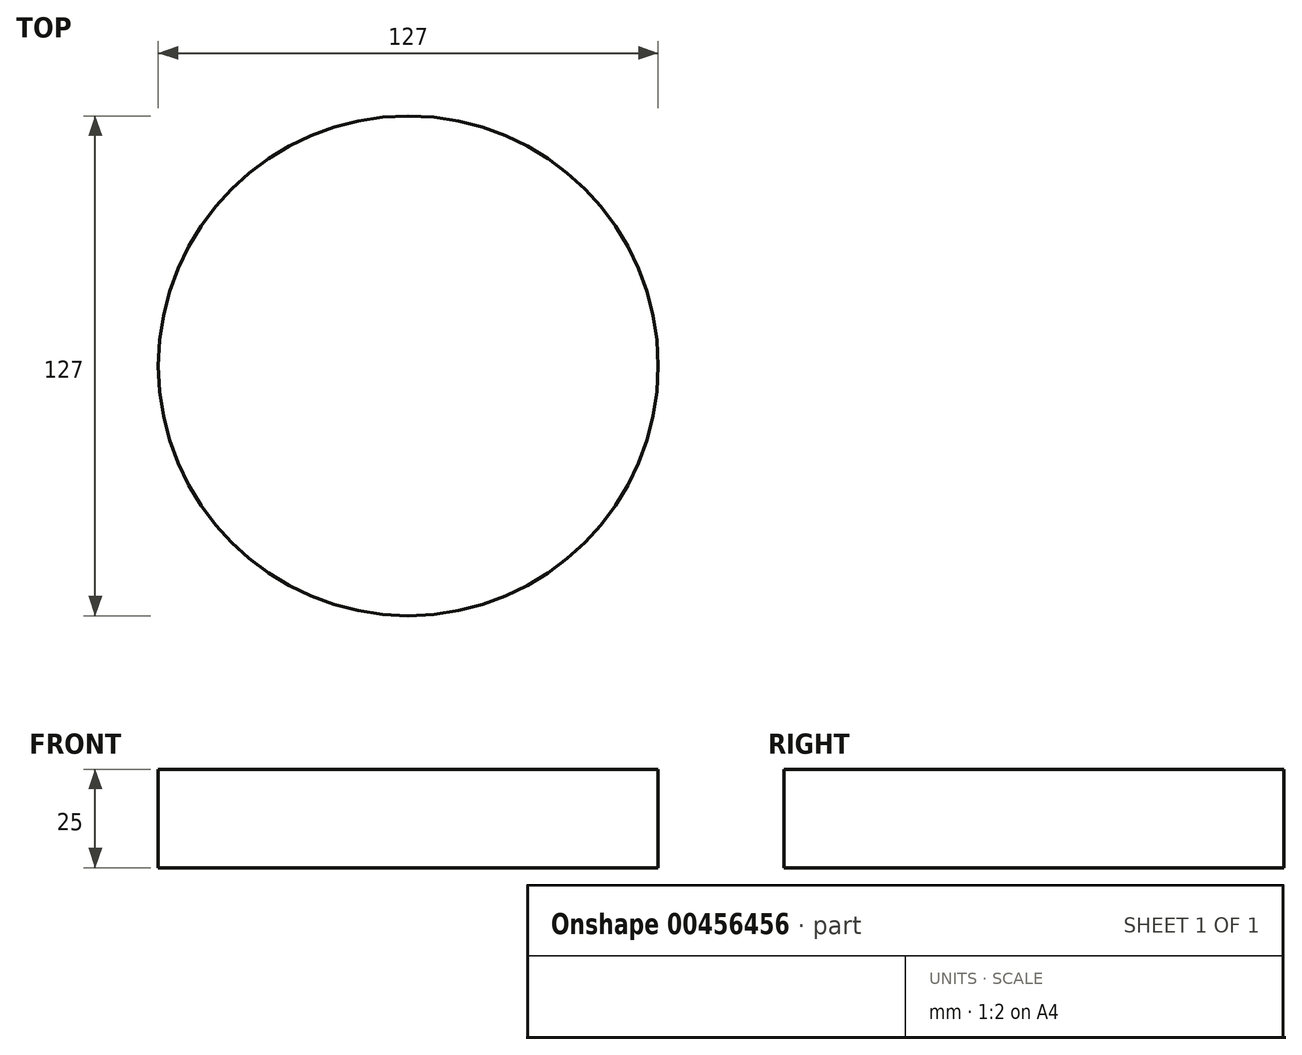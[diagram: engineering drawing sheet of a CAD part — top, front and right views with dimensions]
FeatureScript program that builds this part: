
annotation { "Feature Type Name" : "Feature", "Feature Type Description" : "" }
export const myFeature = defineFeature(function(context is Context, id is Id, definition is map)
    precondition{}
    {
        {
            var Q0;
            Q0=qCreatedBy(makeId("Top.planeOp"),FACE);
            var sketch = newSketch(context, id + "F0", { "sketchPlane" : qUnion([Q0])});
            skCircle(sketch, "E0", {"center": v(0, 0) * mm, "radius": 63.5 * mm});
            skSolve(sketch);
        }
        {
            var Q0;
            Q0=makeQuery(id+"F0.imprint","IMPRINT",FACE,{"disambiguationData":[TD([[makeQuery(id+"F0.imprint","IMPRINT",EDGE,{"derivedFrom":sQuery(id+"F0.wireOp",EDGE,"E0")}),1.0]])]});
            extrude(context, id + "F1", {"entities" : qUnion([Q0]), "depth" : 25 * mm});
        }
    });
